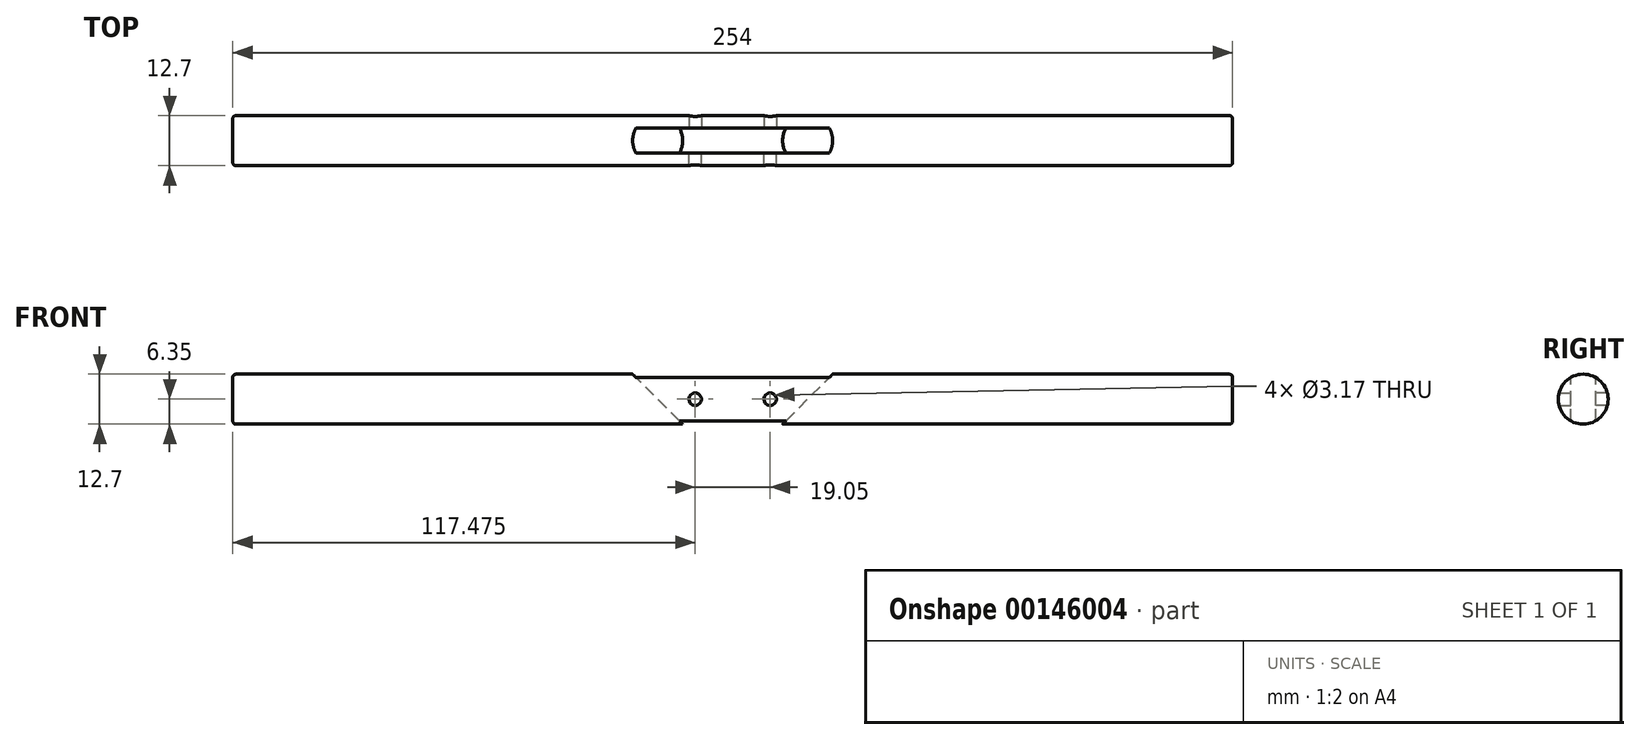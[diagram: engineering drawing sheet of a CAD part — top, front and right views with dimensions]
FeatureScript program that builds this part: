
annotation { "Feature Type Name" : "Feature", "Feature Type Description" : "" }
export const myFeature = defineFeature(function(context is Context, id is Id, definition is map)
    precondition{}
    {
        {
            var Q0;
            Q0=qCreatedBy(makeId("Front.planeOp"),FACE);
            var sketch = newSketch(context, id + "F0", { "sketchPlane" : qUnion([Q0])});
            skPoint(sketch, "E0", {"position": v(0, 0) * mm});
            skPoint(sketch, "E1", {"position": v(0, -12.7) * mm});
            skPoint(sketch, "E2", {"position": v(-25.4, 0) * mm});
            skPoint(sketch, "E3", {"position": v(25.4, 0) * mm});
            skPoint(sketch, "E4", {"position": v(-12.7, -12.7) * mm});
            skPoint(sketch, "E5", {"position": v(12.7, -12.7) * mm});
            skLineSegment(sketch, "E6", {"start": v(-25.4, 0) * mm, "end": v(25.4, 0) * mm, "construction": true});
            skLineSegment(sketch, "E7", {"start": v(-12.7, -12.7) * mm, "end": v(12.7, -12.7) * mm, "construction": true});
            skLineSegment(sketch, "E8", {"start": v(25.4, 0) * mm, "end": v(12.7, -12.7) * mm, "construction": true});
            skLineSegment(sketch, "E9", {"start": v(-25.4, 0) * mm, "end": v(-12.7, -12.7) * mm, "construction": true});
            skLineSegment(sketch, "E10", {"start": v(0, 0) * mm, "end": v(0, -12.7) * mm, "construction": true});
            skPoint(sketch, "E11", {"position": v(0, -6.35) * mm});
            skLineSegment(sketch, "E12", {"start": v(-19.05, -6.35) * mm, "end": v(19.05, -6.35) * mm, "construction": true});
            skPoint(sketch, "E13", {"position": v(-9.53, -6.35) * mm});
            skPoint(sketch, "E14", {"position": v(9.53, -6.35) * mm});
            skLineSegment(sketch, "E15", {"start": v(19.05, -6.35) * mm, "end": v(127, -6.35) * mm, "construction": true});
            skLineSegment(sketch, "E16", {"start": v(-19.05, -6.35) * mm, "end": v(-127, -6.35) * mm, "construction": true});
            skLineSegment(sketch, "E17", {"start": v(-127, 0) * mm, "end": v(-127, -12.7) * mm, "construction": true});
            skSolve(sketch);
        }
        {
            var Q0;
            Q0=sQuery(id+"F0.wireOp",EDGE,"E17");
            cPlane(context, id + "F1", {"entities" : qUnion([Q0]), "cplaneType" : CPlaneType.LINE_ANGLE, "offset" : 25.4 * mm, "angle" : 0 * degree, "width" : 152.4 * mm, "height" : 152.4 * mm});
        }
        {
            var Q0;
            Q0=qCreatedBy(id+"F1.planeOp",FACE);
            var sketch = newSketch(context, id + "F7", { "sketchPlane" : qUnion([Q0])});
            skPoint(sketch, "E18", {"position": v(0, -6.35) * mm});
            skCircle(sketch, "E19", {"center": v(0, -6.35) * mm, "radius": 6.35 * mm});
            skSolve(sketch);
        }
        {
            var Q0;
            Q0=makeQuery(id+"F7.imprint","IMPRINT",FACE,{"disambiguationData":[TD([[makeQuery(id+"F7.imprint","IMPRINT",EDGE,{"derivedFrom":sQuery(id+"F7.wireOp",EDGE,"E19")}),1.0]])]});
            extrude(context, id + "F8", {"entities" : qUnion([Q0]), "oppositeDirection" : true, "depth" : 254 * mm});
        }
        {
            var Q0;
            Q0=sQuery(id+"F0.wireOp",EDGE,"E6");
            cPlane(context, id + "F2", {"entities" : qUnion([Q0]), "cplaneType" : CPlaneType.LINE_ANGLE, "offset" : 25.4 * mm, "angle" : 90 * degree, "width" : 152.4 * mm, "height" : 152.4 * mm});
        }
        {
            var Q0;
            Q0=qCreatedBy(id+"F2.planeOp",FACE);
            var sketch = newSketch(context, id + "F9", { "sketchPlane" : qUnion([Q0])});
            skPoint(sketch, "E20", {"position": v(-25.4, 0) * mm});
            skPoint(sketch, "E21", {"position": v(25.4, 0) * mm});
            skLineSegment(sketch, "E22.bottom", {"start": v(25.4, 3.18) * mm, "end": v(-25.4, 3.18) * mm});
            skLineSegment(sketch, "E22.top", {"start": v(25.4, -3.18) * mm, "end": v(-25.4, -3.18) * mm});
            skLineSegment(sketch, "E22.left", {"start": v(25.4, 3.18) * mm, "end": v(25.4, -3.18) * mm});
            skLineSegment(sketch, "E22.right", {"start": v(-25.4, 3.18) * mm, "end": v(-25.4, -3.18) * mm});
            skPoint(sketch, "E22.middle", {"position": v(0, 0) * mm});
            skSolve(sketch);
        }
        {
            var Q0;
            Q0=sQuery(id+"F0.wireOp",EDGE,"E7");
            cPlane(context, id + "F3", {"entities" : qUnion([Q0]), "cplaneType" : CPlaneType.LINE_ANGLE, "offset" : 25.4 * mm, "angle" : 90 * degree, "width" : 152.4 * mm, "height" : 152.4 * mm});
        }
        {
            var Q0;
            Q0=qCreatedBy(id+"F3.planeOp",FACE);
            var sketch = newSketch(context, id + "F10", { "sketchPlane" : qUnion([Q0])});
            skPoint(sketch, "E23", {"position": v(-12.7, 0) * mm});
            skPoint(sketch, "E24", {"position": v(0, 0) * mm});
            skLineSegment(sketch, "E25.bottom", {"start": v(-12.7, -3.18) * mm, "end": v(12.7, -3.18) * mm});
            skLineSegment(sketch, "E25.top", {"start": v(-12.7, 3.18) * mm, "end": v(12.7, 3.18) * mm});
            skLineSegment(sketch, "E25.left", {"start": v(-12.7, -3.18) * mm, "end": v(-12.7, 3.18) * mm});
            skLineSegment(sketch, "E25.right", {"start": v(12.7, -3.18) * mm, "end": v(12.7, 3.18) * mm});
            skSolve(sketch);
        }
        {
            var Q1;
            Q1=makeQuery(id+"F10.imprint","IMPRINT",FACE,{"disambiguationData":[TD([[makeQuery(id+"F10.imprint","IMPRINT",EDGE,{"derivedFrom":sQuery(id+"F10.wireOp",EDGE,"E25.bottom")}),1.0]])]});
            var Q2;
            Q2=makeQuery(id+"F9.imprint","IMPRINT",FACE,{"disambiguationData":[TD([[makeQuery(id+"F9.imprint","IMPRINT",EDGE,{"derivedFrom":sQuery(id+"F9.wireOp",EDGE,"E22.bottom")}),1.0]])]});
            loft(context, id + "F4", {"operationType" : NewBodyOperationType.REMOVE, "sheetProfilesArray" : [{ "sheetProfileEntities" : qUnion([Q1]) }, { "sheetProfileEntities" : qUnion([Q2]) }]});
        }
        {
            var Q0;
            Q0=sQuery(id+"F0.wireOp",VERTEX,"E13");
            var Q1;
            Q1=sQuery(id+"F0.wireOp",VERTEX,"E14");
            var Q2;
            Q2=makeQuery(id+"F8.opExtrude","SWEPT_BODY",BODY,{"disambiguationData":[OSD([sQuery(id+"F7.wireOp",EDGE,"E19")])]});
            hole(context, id + "F11", {"style" : HoleStyle.SIMPLE, "endStyle" : HoleEndStyle.THROUGH, "holeDiameter" : 3.17 * mm, "locations" : qUnion([Q0, Q1]), "scope" : qUnion([Q2]), "isTappedThrough" : true});
        }
        {
            var Q0;
            Q0=sQuery(id+"F0.wireOp",VERTEX,"E13");
            var Q1;
            Q1=sQuery(id+"F0.wireOp",VERTEX,"E14");
            var Q2;
            Q2=makeQuery(id+"F8.opExtrude","SWEPT_BODY",BODY,{"disambiguationData":[OSD([sQuery(id+"F7.wireOp",EDGE,"E19")])]});
            hole(context, id + "F5", {"style" : HoleStyle.SIMPLE, "endStyle" : HoleEndStyle.THROUGH, "oppositeDirection" : true, "holeDiameter" : 3.17 * mm, "locations" : qUnion([Q0, Q1]), "scope" : qUnion([Q2]), "isTappedThrough" : true});
        }
        {
            var Q0;
            Q0=makeQuery(id+"F8.opExtrude","CAP_EDGE",EDGE,{"disambiguationData":[OSD([sQuery(id+"F7.wireOp",EDGE,"E19")])],"isStart":false});
            var Q1;
            Q1=makeQuery(id+"F8.opExtrude","CAP_EDGE",EDGE,{"disambiguationData":[OSD([sQuery(id+"F7.wireOp",EDGE,"E19")])],"isStart":true});
            fillet(context, id + "F6", {"entities" : qUnion([Q0, Q1]), "radius" : 0.8 * mm, "tangentPropagation" : true, "allowEdgeOverflow" : false});
        }
    });
